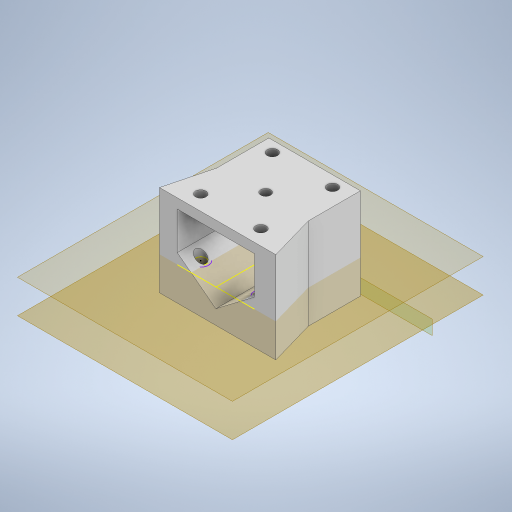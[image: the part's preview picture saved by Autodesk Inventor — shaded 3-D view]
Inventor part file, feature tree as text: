
AUTODESK INVENTOR PART (.ipt)
format: ipt  version: 2024.2 (Build 282272000, 272)  size: 330,752 bytes
history: native  units: mm
features: other x8, sketch x7, extrude x6, projected_geometry x6, reference x5
ambient origin geometry x8: Origin, YZ Plane, XZ Plane, XY Plane, X Axis, Y Axis, Z Axis, Center Point
bodies: Body1 (feature_tree)
feature tree (32):
  other  "Твердое тело1"
  other  "РабПлоскость2"
  extrude  "Выдавливание1"  Depth=1.0mm
  other  "РабПлоскость3"
  extrude  "Выдавливание3"  Depth=1.0mm
  other  "РабПлоскость4"
  extrude  "дырки"  Depth=4.426mm
  sketch  "Эскиз4"
  other  "РабПлоскость5"
  extrude  "Выдавливание5"  Depth=30.0mm TaperAngle=0.0deg
  extrude  "Выдавливание6"  TaperAngle=0.0deg  [1 undecoded]
  extrude  "Выдавливание7"  Depth=9.0mm
  sketch  "Эскиз1"
  reference  "Ссылка1"
  reference  "Ссылка2"
  reference  "Ссылка3"
  reference  "Ссылка4"
  sketch  "Эскиз2"
  sketch  "Эскиз3"
  projected_geometry  "Спроецированная петля1"
  projected_geometry  "Спроецированная петля2"
  sketch  "Эскиз5"
  projected_geometry  "Спроецированная петля3"
  projected_geometry  "Спроецированная петля4"
  sketch  "Эскиз6"
  projected_geometry  "Спроецированная петля5"
  projected_geometry  "Спроецированная петля6"
  reference  "Ссылка5"
  sketch  "Эскиз7"
  other  "<userpath>\Documents\Artist\3D\каретка.iam"
  other  "каретка.iam"
  other  "ANY:5"
note: 1 required parameter value undecoded (feature->parameter linkage not recoverable at this tier; creation-order binding heuristic only, values carry confidence <= 0.55)
